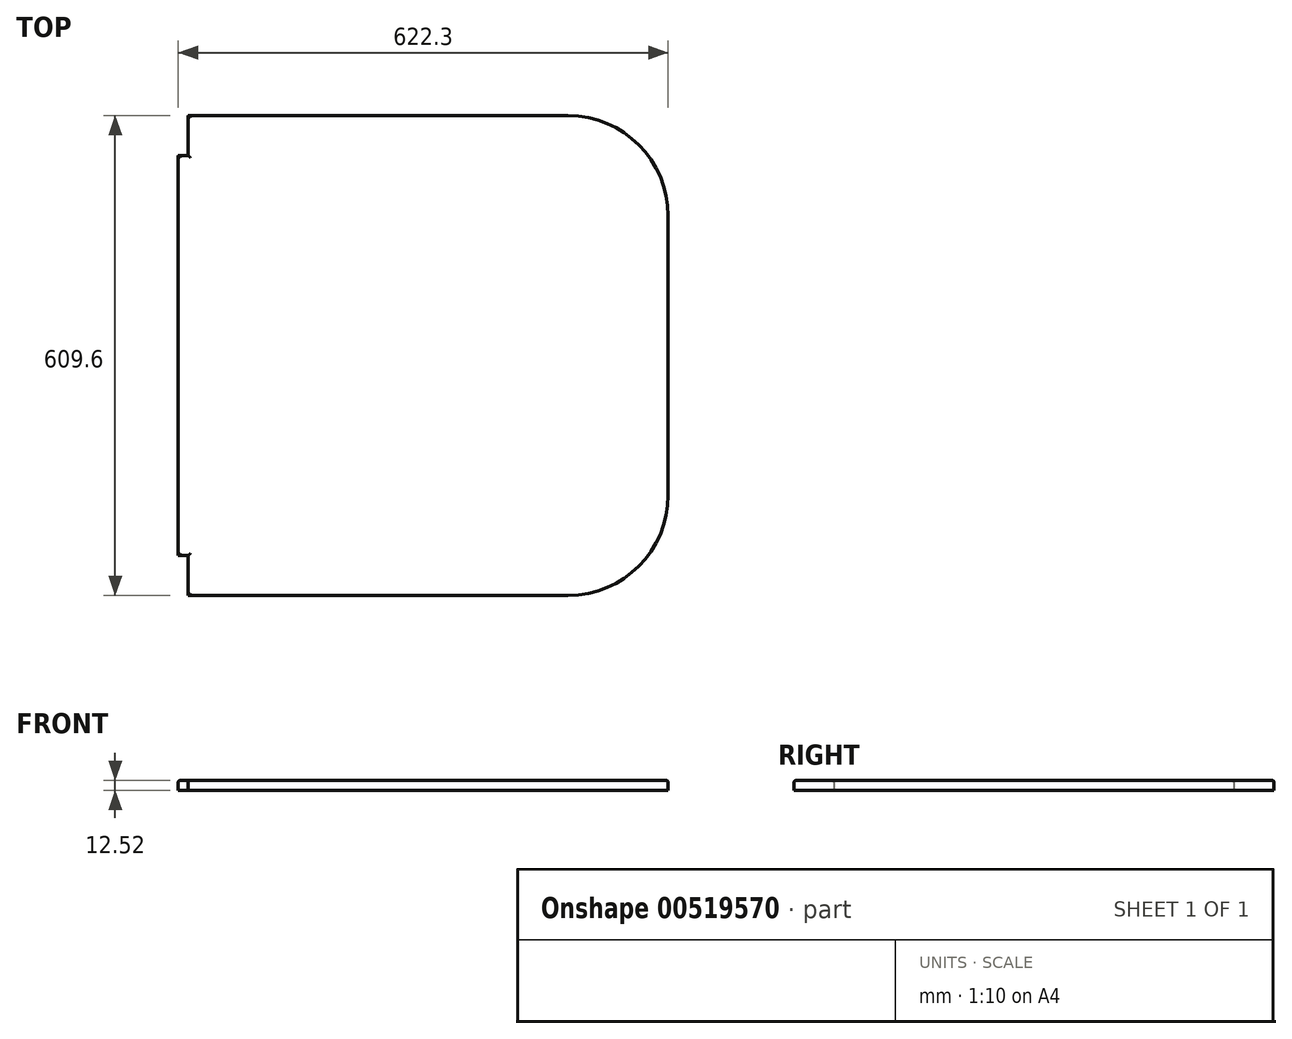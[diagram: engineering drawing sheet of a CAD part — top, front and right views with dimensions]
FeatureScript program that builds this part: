
annotation { "Feature Type Name" : "Feature", "Feature Type Description" : "" }
export const myFeature = defineFeature(function(context is Context, id is Id, definition is map)
    precondition{}
    {
        {
            var Q0;
            Q0=qCreatedBy(makeId("Top.planeOp"),FACE);
            var sketch = newSketch(context, id + "F0", { "sketchPlane" : qUnion([Q0])});
            skLineSegment(sketch, "E0.bottom", {"start": v(-557.22, 605.82) * mm, "end": v(-74.62, 605.82) * mm});
            skLineSegment(sketch, "E0.top", {"start": v(-557.22, -3.78) * mm, "end": v(-74.62, -3.78) * mm});
            skLineSegment(sketch, "E0.left", {"start": v(-557.22, 605.82) * mm, "end": v(-557.22, -3.78) * mm});
            skLineSegment(sketch, "E0.right", {"start": v(52.38, 478.82) * mm, "end": v(52.38, 123.22) * mm});
            skLineSegment(sketch, "E1", {"start": v(-557.22, 555.02) * mm, "end": v(-569.92, 555.02) * mm});
            skLineSegment(sketch, "E2", {"start": v(-569.92, 555.02) * mm, "end": v(-569.92, 47.02) * mm});
            skLineSegment(sketch, "E3", {"start": v(-569.92, 47.02) * mm, "end": v(-557.22, 47.02) * mm});
            skPoint(sketch, "E4.visualSharp", {"position": v(52.38, 605.82) * mm});
            skArc(sketch, "E4.filletArc", {"start": v(52.38, 478.82) * mm, "mid": v(15.18, 568.62) * mm, "end": v(-74.62, 605.82) * mm});
            skPoint(sketch, "E5.visualSharp", {"position": v(52.38, -3.78) * mm});
            skArc(sketch, "E5.filletArc", {"start": v(-74.62, -3.78) * mm, "mid": v(15.18, 33.42) * mm, "end": v(52.38, 123.22) * mm});
            skSolve(sketch);
        }
        {
            var Q0;
            Q0 = qSketchRegion(id + "F0", true);
            extrude(context, id + "F1", {"entities" : qUnion([Q0]), "depth" : 12.52 * mm, "offsetDistance" : 25.4 * mm});
        }
        {
            var Q0;
            Q0=makeQuery(id+"F1.opExtrude","CAP_FACE",FACE,{"disambiguationData":[OSD([sQuery(id+"F0.wireOp",EDGE,"E0.bottom"),sQuery(id+"F0.wireOp",EDGE,"E0.top"),sQuery(id+"F0.wireOp",EDGE,"E0.left"),sQuery(id+"F0.wireOp",EDGE,"E0.right"),sQuery(id+"F0.wireOp",EDGE,"E1"),sQuery(id+"F0.wireOp",EDGE,"E2"),sQuery(id+"F0.wireOp",EDGE,"E3")])],"isStart":false});
            fillet(context, id + "F2", {"entities" : qUnion([Q0]), "radius" : 2.45 * mm, "tangentPropagation" : true, "allowEdgeOverflow" : false});
        }
    });
